# Revit family: Lid Pepper Grill
name_source: partatom
category: Furniture
units: mm (PartAtom-declared; Revit-internal decimal feet)

## family parameters
Always vertical = Yes
Cut with Voids When Loaded = No
Enable Cutting in Views = No
OmniClass Number = 23.11.27.00
Render Appearance Source = Family Geometry
Room Calculation Point = No
Shared = No
Work Plane-Based = No

## types (1)
- 8079664 Black
    BIMobject category = Other Furniture
    Body material = Hags - Steel - Powder coated - Black
    Default Elevation = 0 mm  [stored 0 ft]
    Description = Lid Grill Pepper
    Edition number = 1
    IFC Classification = Object
    Manufacturer = Hags
    Manufacturer name = HAGS
    Model = 8091125
    OmniClass Code = 23-11 27 00
    OmniClass Description = Landscaping
    Product Guid = 81941e82-575a-4e68-9d9e-8cba3ca19888
    Product SKU = NaN
    Product data url = https://bimobject.com
    Product name = Lid Grill Pepper
Grill Pepper
Grill Pepper
Grill Pepper
df
    Product url = https://hags.se
    QR code = https://bimobject.com
    URL = https://www.hags.com
    Uniclass 1.4 Code = JN
    Uniclass 1.4 Description = Furniture/Equipment

note: [stored X ft] marks values corroborated as IEEE doubles in the binary element streams (Revit-internal decimal feet)

## geometry (parser evidence)
native form markers: Sweep x3
no freeform markers — native parametric forms only
